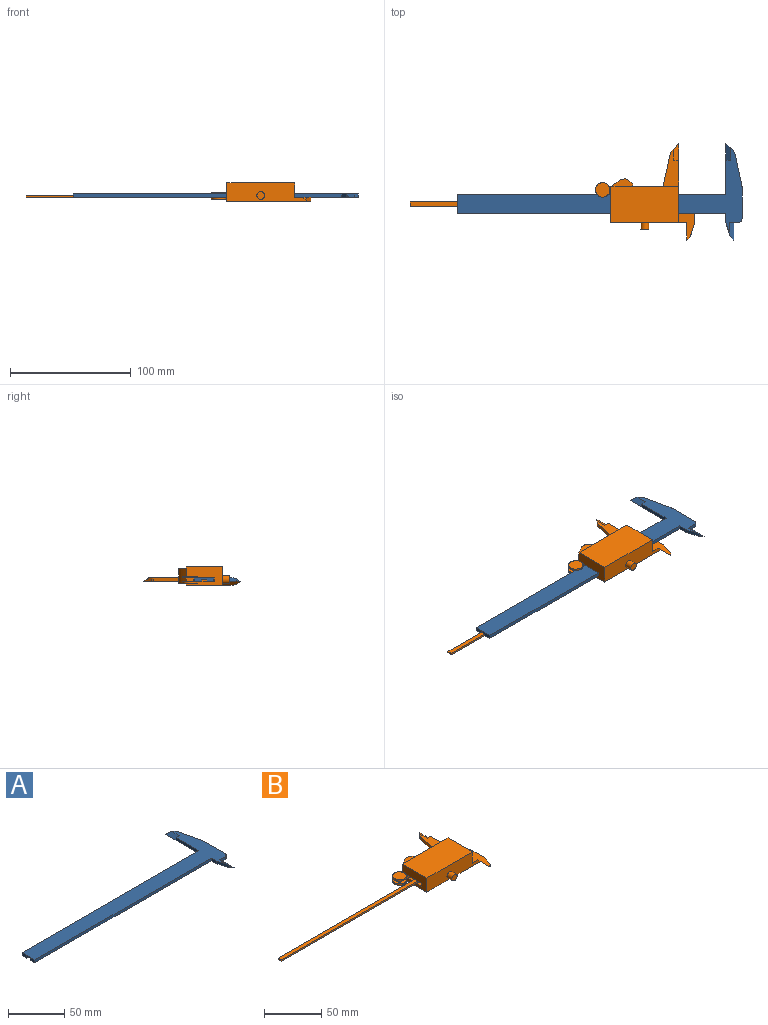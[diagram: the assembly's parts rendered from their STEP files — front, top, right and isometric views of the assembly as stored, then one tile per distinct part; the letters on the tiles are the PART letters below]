
ASSEMBLY  parts=2 mates=2
PART A: 23 faces, bbox 236x79.8x3 mm
  f0: plane 7x2.99mm, normal (-1,0,0), area 20.9mm2, adj f1,f5,f20,f22
  f1: plane 236x79.76mm, normal (0,0,-1), area 3418.3mm2, adj f0,f2,f3,f4,f6,f7,f8,f9
  f2: plane 14.75x3.96mm, normal (0.6,0,0.8), area 62.8mm2, adj f1,f5,f8,f21,f22
  f3: plane 28.5x2.99mm, normal (-1,0,0), area 85.1mm2, adj f1,f5,f13,f16
  f4: plane 4.17x1.58mm, normal (-1,0,0), area 6.6mm2, adj f1,f17,f18,f19
  f5: plane 236x70.08mm, normal (0,0,1), area 4247.8mm2, adj f0,f2,f3,f6,f7,f8,f9,f10
  f6: plane 6.35x5.94mm, normal (0.68,0.73,0), area 17.5mm2, adj f1,f5,f11,f14
  f7: plane 26.47x2.99mm, normal (1,0,0), area 79mm2, adj f1,f5,f9,f12
  f8: plane 7.71x2.99mm, normal (0,-1,0), area 17.1mm2, adj f1,f2,f5,f9
  f9: cylinder r=3mm len=3mm, axis (0,0,1), area 14.1mm2, adj f1,f5,f7,f8
  f10: plane 25.95x5.56mm, normal (0.98,0.21,0), area 79.2mm2, adj f1,f5,f11,f12
  f11: cylinder r=5mm len=2.99mm, axis (0,0,-1), area 9.1mm2, adj f1,f5,f6,f10
  f12: cylinder r=5mm len=2.99mm, axis (0,0,1), area 3.2mm2, adj f1,f5,f7,f10
  f13: plane 4.12x2.99mm, normal (0,1,0), area 6.1mm2, adj f3,f5,f14
  f14: plane 13.51x4.12mm, normal (-0.59,0,0.81), area 58.9mm2, adj f1,f5,f6,f13
  f15: plane 16x2.99mm, normal (-1,0,0), area 41.2mm2, adj f1,f5,f16,f17,f18,f19,f20
  f16: plane 222.5x2.99mm, normal (0,1,0), area 664.2mm2, adj f1,f3,f5,f15
  f17: plane 222.5x1.58mm, normal (0,-1,0), area 352mm2, adj f1,f4,f15,f18
  f18: plane 222.5x4.17mm, normal (0,0,-1), area 927.4mm2, adj f4,f15,f17,f19
  f19: plane 222.5x1.58mm, normal (0,1,0), area 352mm2, adj f1,f4,f15,f18
  f20: plane 222.5x2.99mm, normal (0,-1,0), area 664.2mm2, adj f0,f1,f5,f15
  f21: plane 3x2.75mm, normal (-0.68,-0.74,0), area 4.6mm2, adj f1,f2,f22
  f22: plane 12x3.75mm, normal (-0.95,-0.3,0), area 36.4mm2, adj f0,f1,f2,f5,f21
PART B: 50 faces, bbox 236x79.8x15 mm
  f0: plane 69.5x38.85mm, normal (0,0,-1), area 1925.1mm2, adj f6,f12,f14,f15,f16,f19,f22,f23
  f1: plane 166.5x4mm, normal (0,0,-1), area 666mm2, adj f2,f3,f4,f15
  f2: plane 4x1.5mm, normal (-1,0,0), area 6mm2, adj f1,f3,f4,f5
  f3: plane 222.5x1.5mm, normal (0,-1,0), area 333.7mm2, adj f1,f2,f5,f6,f18
  f4: plane 222.5x1.5mm, normal (0,1,0), area 333.7mm2, adj f1,f2,f5,f6,f7
  f5: plane 222.5x4mm, normal (0,0,1), area 890mm2, adj f2,f3,f4,f6
  f6: plane 51.5x15mm, normal (1,0,0), area 411.3mm2, adj f0,f3,f4,f5,f7,f11,f12,f13
  f7: plane 56x6.25mm, normal (0,0,1), area 350mm2, adj f4,f6,f15,f42
  f8: plane 6.17x1.72mm, normal (0,0,-1), area 7mm2, adj f15,f33,f34,f39
  f9: plane 6.17x1.72mm, normal (0,0,1), area 7mm2, adj f15,f33,f34,f37
  f10: plane 12x0.49mm, normal (0,1,0), area 5.9mm2, adj f29,f30,f31,f32
  f11: plane 35.01x13mm, normal (0,0,-1), area 296.6mm2, adj f6,f12,f24,f25,f26,f27
  f12: plane 56x15mm, normal (0,1,0), area 573.2mm2, adj f0,f6,f11,f15,f17,f21,f25,f29
  f13: plane 13.5x0.18mm, normal (0,1,0), area 2.4mm2, adj f6,f14,f18,f20
  f14: plane 14.25x3mm, normal (1,0,0), area 42.5mm2, adj f0,f13,f18,f20,f23,f49
  f15: plane 30x15mm, normal (-1,0,0), area 382mm2, adj f0,f1,f7,f8,f9,f12,f16,f17
  f16: plane 66.73x15mm, normal (0,-1,0), area 833mm2, adj f0,f6,f15,f17,f18,f22,f45
  f17: plane 56x30mm, normal (0,0,1), area 1680mm2, adj f6,f12,f15,f16
  f18: plane 69.5x27.75mm, normal (0,0,1), area 584.8mm2, adj f3,f6,f13,f14,f15,f16,f22,f44
  f19: plane 7.5x2.82mm, normal (0,1,0), area 21.2mm2, adj f0,f20,f23,f47
  f20: plane 13.5x7.5mm, normal (0,0,1), area 60.7mm2, adj f6,f13,f14,f19,f23,f47
  f21: plane 30.61x13mm, normal (0,0,1), area 250mm2, adj f6,f12,f24,f25,f26,f27,f28
  f22: plane 14.75x3.98mm, normal (-0.6,0,-0.8), area 63.1mm2, adj f0,f16,f18,f48,f49
  f23: cylinder r=3mm len=3mm, axis (0,0,1), area 13.3mm2, adj f0,f14,f19,f20
  f24: plane 6.03x5.64mm, normal (-0.73,0.68,0), area 15.6mm2, adj f11,f21,f26,f27
  f25: plane 26.69x6.14mm, normal (-0.97,0.22,0), area 81.8mm2, adj f11,f12,f21,f26
  f26: cylinder r=5mm len=2.99mm, axis (0,0,-1), area 7.8mm2, adj f11,f21,f24,f25
  f27: plane 13.51x4.12mm, normal (0.59,0,0.81), area 57.5mm2, adj f11,f21,f24,f28
  f28: plane 4.12x2.99mm, normal (0,1,0), area 6.1mm2, adj f6,f21,f27
  f29: plane 19.37x6.75mm, normal (0,0,1), area 70.7mm2, adj f10,f12,f31,f32
  f30: plane 19.37x6.75mm, normal (0,0,-1), area 70.7mm2, adj f10,f12,f31,f32
  f31: extruded ~12x11mm, area 152mm2, adj f10,f15,f29,f30,f33
  f32: extruded ~12x7.51mm, area 119mm2, adj f10,f12,f29,f30
  f33: plane 10x3mm, normal (0,1,0), area 30mm2, adj f8,f9,f31,f35,f36,f41
  f34: plane 10x3mm, normal (0,-1,0), area 30mm2, adj f8,f9,f15,f35,f36,f41
  f35: plane 6.17x3mm, normal (-1,0,0), area 18.5mm2, adj f33,f34,f36,f41
  f36: plane 12x11.15mm, normal (0,0,-1), area 58.4mm2, adj f33,f34,f35,f37
  f37: cylinder r=6mm len=12mm, axis (0,0,-1), area 56.5mm2, adj f9,f36,f38
  f38: plane 12x12mm, normal (0,0,1), area 113.1mm2, adj f37
  f39: cylinder r=6mm len=12mm, axis (0,0,1), area 56.5mm2, adj f8,f40,f41
  f40: plane 12x12mm, normal (0,0,-1), area 113.1mm2, adj f39
  f41: plane 12x11.15mm, normal (0,0,1), area 58.4mm2, adj f33,f34,f35,f39
  f42: plane 56x3mm, normal (0,-1,0), area 168mm2, adj f6,f7,f15,f43
  f43: plane 56x16.5mm, normal (0,0,-1), area 924mm2, adj f6,f15,f42,f44
  f44: plane 56x3mm, normal (0,1,0), area 168mm2, adj f6,f15,f18,f43
  f45: cylinder r=3.25mm len=6.5mm, axis (0,1,0), area 122.5mm2, adj f16,f46
  f46: plane 6.5x6.5mm, normal (0,-1,0), area 33.2mm2, adj f45
  f47: cylinder r=3mm len=3mm, axis (0,0,1), area 13.3mm2, adj f0,f6,f19,f20
  f48: plane 3x2.75mm, normal (0.68,-0.74,0), area 4.6mm2, adj f18,f22,f49
  f49: plane 12x3.75mm, normal (0.95,-0.3,0), area 36.5mm2, adj f0,f14,f18,f22,f48
PLACE A t=(38.85,1.08,-0.36)mm
PLACE B t=(-0.21,1,-0.36)mm fixed
MATE planar A.f19 <-> B.f3  axis (0,1,0) through (32.1,-1,0.43)mm
MATE planar A.f1 <-> B.f1  axis (0,0,-1) through (59.02,3.43,-0.36)mm
